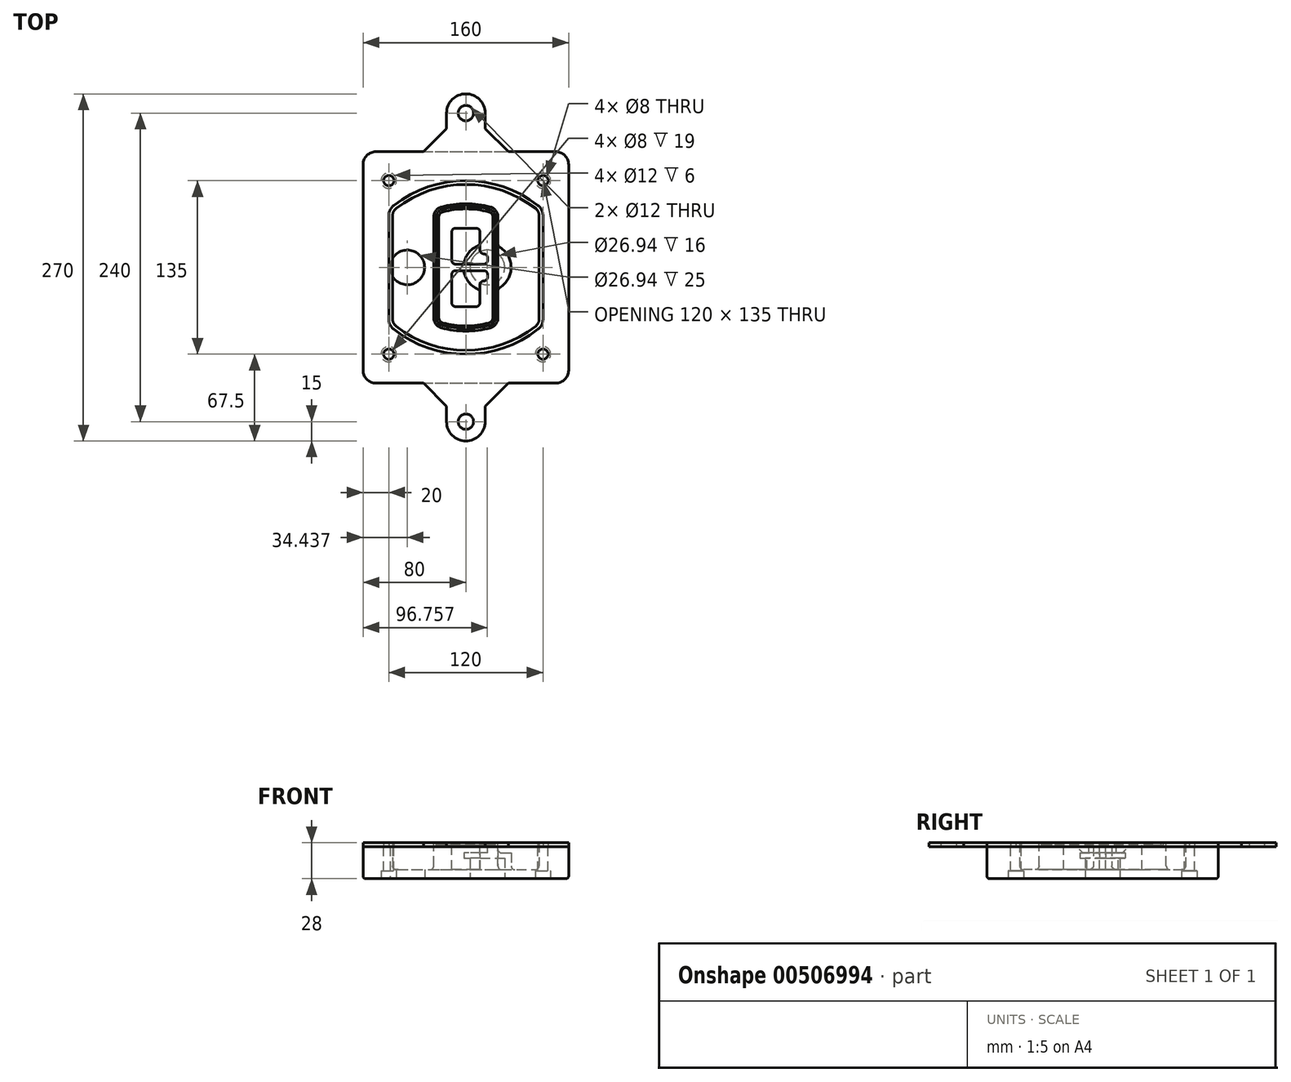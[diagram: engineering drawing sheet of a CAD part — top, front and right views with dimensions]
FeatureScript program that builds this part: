
annotation { "Feature Type Name" : "Feature", "Feature Type Description" : "" }
export const myFeature = defineFeature(function(context is Context, id is Id, definition is map)
    precondition{}
    {
        {
            var Q0;
            Q0=qCreatedBy(makeId("Top.planeOp"),FACE);
            var sketch = newSketch(context, id + "F0", { "sketchPlane" : qUnion([Q0])});
            skPoint(sketch, "E0.rect.middle", {"position": v(0, 0) * mm});
            skLineSegment(sketch, "E1.bottom", {"start": v(-70, -90) * mm, "end": v(70, -90) * mm});
            skLineSegment(sketch, "E1.top", {"start": v(-70, 90) * mm, "end": v(70, 90) * mm});
            skLineSegment(sketch, "E1.left", {"start": v(-80, -80) * mm, "end": v(-80, 80) * mm});
            skLineSegment(sketch, "E1.right", {"start": v(80, -80) * mm, "end": v(80, 80) * mm});
            skLineSegment(sketch, "E2", {"start": v(-80, 90) * mm, "end": v(80, -90) * mm, "construction": true});
            skLineSegment(sketch, "E3", {"start": v(80, 90) * mm, "end": v(-80, -90) * mm, "construction": true});
            skCircle(sketch, "E4", {"center": v(-60, 67.5) * mm, "radius": 4 * mm});
            skCircle(sketch, "E5", {"center": v(60, 67.5) * mm, "radius": 4 * mm});
            skCircle(sketch, "E6", {"center": v(60, -67.5) * mm, "radius": 4 * mm});
            skCircle(sketch, "E7", {"center": v(-60, -67.5) * mm, "radius": 4 * mm});
            skLineSegment(sketch, "E8", {"start": v(-60, 67.5) * mm, "end": v(60, 67.5) * mm, "construction": true});
            skLineSegment(sketch, "E9", {"start": v(60, 67.5) * mm, "end": v(60, -67.5) * mm, "construction": true});
            skLineSegment(sketch, "E10", {"start": v(60, -67.5) * mm, "end": v(-60, -67.5) * mm, "construction": true});
            skLineSegment(sketch, "E11", {"start": v(-60, -67.5) * mm, "end": v(-60, 67.5) * mm, "construction": true});
            skLineSegment(sketch, "E12", {"start": v(-60, 40.3) * mm, "end": v(-60, -40.3) * mm});
            skLineSegment(sketch, "E13", {"start": v(60, 40.3) * mm, "end": v(60, -40.3) * mm});
            skArc(sketch, "E14", {"start": v(56.15, 48.18) * mm, "mid": v(0, 67.5) * mm, "end": v(-56.15, 48.18) * mm});
            skArc(sketch, "E15", {"start": v(-56.15, -48.18) * mm, "mid": v(0, -67.5) * mm, "end": v(56.15, -48.18) * mm});
            skLineSegment(sketch, "E16", {"start": v(-60, 0) * mm, "end": v(60, 0) * mm, "construction": true});
            skPoint(sketch, "E17.visualSharp", {"position": v(-60, -45) * mm});
            skArc(sketch, "E17.filletArc", {"start": v(-60, -40.3) * mm, "mid": v(-58.99, -44.68) * mm, "end": v(-56.15, -48.18) * mm});
            skPoint(sketch, "E18.visualSharp", {"position": v(-60, 45) * mm});
            skArc(sketch, "E18.filletArc", {"start": v(-56.15, 48.18) * mm, "mid": v(-58.99, 44.68) * mm, "end": v(-60, 40.3) * mm});
            skPoint(sketch, "E19.visualSharp", {"position": v(60, 45) * mm});
            skArc(sketch, "E19.filletArc", {"start": v(60, 40.3) * mm, "mid": v(58.99, 44.68) * mm, "end": v(56.15, 48.18) * mm});
            skPoint(sketch, "E20.visualSharp", {"position": v(60, -45) * mm});
            skArc(sketch, "E20.filletArc", {"start": v(56.15, -48.18) * mm, "mid": v(58.99, -44.68) * mm, "end": v(60, -40.3) * mm});
            skPoint(sketch, "E21.visualSharp", {"position": v(-80, 90) * mm});
            skArc(sketch, "E21.filletArc", {"start": v(-70, 90) * mm, "mid": v(-77.07, 87.07) * mm, "end": v(-80, 80) * mm});
            skPoint(sketch, "E22.visualSharp", {"position": v(80, 90) * mm});
            skArc(sketch, "E22.filletArc", {"start": v(80, 80) * mm, "mid": v(77.07, 87.07) * mm, "end": v(70, 90) * mm});
            skPoint(sketch, "E23.visualSharp", {"position": v(80, -90) * mm});
            skArc(sketch, "E23.filletArc", {"start": v(70, -90) * mm, "mid": v(77.07, -87.07) * mm, "end": v(80, -80) * mm});
            skPoint(sketch, "E24.visualSharp", {"position": v(-80, -90) * mm});
            skArc(sketch, "E24.filletArc", {"start": v(-80, -80) * mm, "mid": v(-77.07, -87.07) * mm, "end": v(-70, -90) * mm});
            skArc(sketch, "E25.0", {"start": v(57, 40.3) * mm, "mid": v(56.3, 43.36) * mm, "end": v(54.3, 45.81) * mm});
            skLineSegment(sketch, "E25.1", {"start": v(57, 40.3) * mm, "end": v(57, -40.3) * mm});
            skArc(sketch, "E25.2", {"start": v(54.3, -45.81) * mm, "mid": v(56.3, -43.36) * mm, "end": v(57, -40.3) * mm});
            skArc(sketch, "E25.3", {"start": v(-54.3, -45.81) * mm, "mid": v(0, -64.5) * mm, "end": v(54.3, -45.81) * mm});
            skArc(sketch, "E25.4", {"start": v(-57, -40.3) * mm, "mid": v(-56.3, -43.36) * mm, "end": v(-54.3, -45.81) * mm});
            skArc(sketch, "E25.5", {"start": v(54.3, 45.81) * mm, "mid": v(0, 64.5) * mm, "end": v(-54.3, 45.81) * mm});
            skLineSegment(sketch, "E25.6", {"start": v(-57, 40.3) * mm, "end": v(-57, -40.3) * mm});
            skArc(sketch, "E25.7", {"start": v(-54.3, 45.81) * mm, "mid": v(-56.3, 43.36) * mm, "end": v(-57, 40.3) * mm});
            skArc(sketch, "E26.0", {"start": v(-58.62, 51.33) * mm, "mid": v(-62.58, 46.43) * mm, "end": v(-64, 40.3) * mm});
            skArc(sketch, "E26.1", {"start": v(58.62, 51.33) * mm, "mid": v(0, 71.5) * mm, "end": v(-58.62, 51.33) * mm});
            skArc(sketch, "E26.2", {"start": v(64, 40.3) * mm, "mid": v(62.58, 46.43) * mm, "end": v(58.62, 51.33) * mm});
            skLineSegment(sketch, "E26.3", {"start": v(64, 40.3) * mm, "end": v(64, -40.3) * mm});
            skArc(sketch, "E26.4", {"start": v(58.62, -51.33) * mm, "mid": v(62.58, -46.43) * mm, "end": v(64, -40.3) * mm});
            skLineSegment(sketch, "E26.5", {"start": v(-64, 40.3) * mm, "end": v(-64, -40.3) * mm});
            skArc(sketch, "E26.6", {"start": v(-58.62, -51.33) * mm, "mid": v(0, -71.5) * mm, "end": v(58.62, -51.33) * mm});
            skArc(sketch, "E26.7", {"start": v(-64, -40.3) * mm, "mid": v(-62.58, -46.43) * mm, "end": v(-58.62, -51.33) * mm});
            skSolve(sketch);
        }
        {
            var Q0;
            Q0=makeQuery(id+"F0.imprint","IMPRINT",FACE,{"disambiguationData":[TD([[makeQuery(id+"F0.imprint","IMPRINT",EDGE,{"derivedFrom":sQuery(id+"F0.wireOp",EDGE,"E1.bottom")}),1.0]])]});
            var Q1;
            Q1=makeQuery(id+"F0.imprint","IMPRINT",FACE,{"disambiguationData":[TD([[makeQuery(id+"F0.imprint","IMPRINT",EDGE,{"derivedFrom":sQuery(id+"F0.wireOp",EDGE,"E12")}),1.0]])]});
            var Q2;
            Q2=makeQuery(id+"F0.imprint","IMPRINT",FACE,{"disambiguationData":[TD([[makeQuery(id+"F0.imprint","IMPRINT",EDGE,{"derivedFrom":sQuery(id+"F0.wireOp",EDGE,"E25.0")}),1.0]])]});
            var Q3;
            Q3=makeQuery(id+"F0.imprint","IMPRINT",FACE,{"disambiguationData":[TD([[makeQuery(id+"F0.imprint","IMPRINT",EDGE,{"derivedFrom":sQuery(id+"F0.wireOp",EDGE,"E12")}),-1.0]])]});
            extrude(context, id + "F1", {"entities" : qUnion([Q0, Q1, Q2, Q3]), "oppositeDirection" : true, "depth" : 25 * mm});
        }
        {
            var Q0;
            Q0=makeQuery(id+"F0.imprint","IMPRINT",FACE,{"disambiguationData":[TD([[makeQuery(id+"F0.imprint","IMPRINT",EDGE,{"derivedFrom":sQuery(id+"F0.wireOp",EDGE,"E12")}),1.0]])]});
            extrude(context, id + "F2", {"entities" : qUnion([Q0]), "operationType" : NewBodyOperationType.ADD, "depth" : 3 * mm});
        }
        {
            var Q0;
            Q0=makeQuery(id+"F0.imprint","IMPRINT",FACE,{"disambiguationData":[TD([[makeQuery(id+"F0.imprint","IMPRINT",EDGE,{"derivedFrom":sQuery(id+"F0.wireOp",EDGE,"E25.0")}),1.0]])]});
            extrude(context, id + "F3", {"entities" : qUnion([Q0]), "operationType" : NewBodyOperationType.REMOVE, "oppositeDirection" : true, "depth" : 18 * mm});
        }
        {
            var Q0;
            Q0=makeQuery(id+"F2.opExtrude","CAP_FACE",FACE,{"disambiguationData":[OSD([sQuery(id+"F0.wireOp",EDGE,"E12"),sQuery(id+"F0.wireOp",EDGE,"E13"),sQuery(id+"F0.wireOp",EDGE,"E14"),sQuery(id+"F0.wireOp",EDGE,"E15"),sQuery(id+"F0.wireOp",EDGE,"E17.filletArc"),sQuery(id+"F0.wireOp",EDGE,"E18.filletArc"),sQuery(id+"F0.wireOp",EDGE,"E19.filletArc"),sQuery(id+"F0.wireOp",EDGE,"E20.filletArc"),sQuery(id+"F0.wireOp",EDGE,"E25.0"),sQuery(id+"F0.wireOp",EDGE,"E25.1"),sQuery(id+"F0.wireOp",EDGE,"E25.2"),sQuery(id+"F0.wireOp",EDGE,"E25.3"),sQuery(id+"F0.wireOp",EDGE,"E25.4"),sQuery(id+"F0.wireOp",EDGE,"E25.5"),sQuery(id+"F0.wireOp",EDGE,"E25.6"),sQuery(id+"F0.wireOp",EDGE,"E25.7")])],"isStart":false});
            var sketch = newSketch(context, id + "F4", { "sketchPlane" : qUnion([Q0])});
            skArc(sketch, "E27.0", {"start": v(-19.08, -46.97) * mm, "mid": v(0, -49.5) * mm, "end": v(19.08, -46.97) * mm});
            skArc(sketch, "E28.0", {"start": v(19.08, 46.97) * mm, "mid": v(0, 49.5) * mm, "end": v(-19.08, 46.97) * mm});
            skLineSegment(sketch, "E29", {"start": v(-25, 39.25) * mm, "end": v(-25, -39.25) * mm});
            skLineSegment(sketch, "E30", {"start": v(25, 39.25) * mm, "end": v(25, -39.25) * mm});
            skLineSegment(sketch, "E31", {"start": v(-25, 45.1) * mm, "end": v(25, 45.1) * mm, "construction": true});
            skLineSegment(sketch, "E32", {"start": v(-25, -45.1) * mm, "end": v(25, -45.1) * mm, "construction": true});
            skPoint(sketch, "E33.visualSharp", {"position": v(-25, 45.1) * mm});
            skArc(sketch, "E33.filletArc", {"start": v(-19.08, 46.97) * mm, "mid": v(-23.35, 44.11) * mm, "end": v(-25, 39.25) * mm});
            skPoint(sketch, "E34.visualSharp", {"position": v(25, 45.1) * mm});
            skArc(sketch, "E34.filletArc", {"start": v(25, 39.25) * mm, "mid": v(23.35, 44.11) * mm, "end": v(19.08, 46.97) * mm});
            skPoint(sketch, "E35.visualSharp", {"position": v(25, -45.1) * mm});
            skArc(sketch, "E35.filletArc", {"start": v(19.08, -46.97) * mm, "mid": v(23.35, -44.11) * mm, "end": v(25, -39.25) * mm});
            skPoint(sketch, "E36.visualSharp", {"position": v(-25, -45.1) * mm});
            skArc(sketch, "E36.filletArc", {"start": v(-25, -39.25) * mm, "mid": v(-23.35, -44.11) * mm, "end": v(-19.08, -46.97) * mm});
            skArc(sketch, "E37.0", {"start": v(54.3, 45.81) * mm, "mid": v(0, 64.5) * mm, "end": v(-54.3, 45.81) * mm});
            skArc(sketch, "E37.1", {"start": v(-54.3, 45.81) * mm, "mid": v(-56.3, 43.36) * mm, "end": v(-57, 40.3) * mm});
            skLineSegment(sketch, "E37.2", {"start": v(-57, 40.3) * mm, "end": v(-57, -40.3) * mm});
            skArc(sketch, "E37.3", {"start": v(-57, -40.3) * mm, "mid": v(-56.3, -43.36) * mm, "end": v(-54.3, -45.81) * mm});
            skArc(sketch, "E37.4", {"start": v(-54.3, -45.81) * mm, "mid": v(0, -64.5) * mm, "end": v(54.3, -45.81) * mm});
            skArc(sketch, "E37.5", {"start": v(54.3, -45.81) * mm, "mid": v(56.3, -43.36) * mm, "end": v(57, -40.3) * mm});
            skLineSegment(sketch, "E37.6", {"start": v(57, 40.3) * mm, "end": v(57, -40.3) * mm});
            skArc(sketch, "E37.7", {"start": v(57, 40.3) * mm, "mid": v(56.3, 43.36) * mm, "end": v(54.3, 45.81) * mm});
            skLineSegment(sketch, "E38.0", {"start": v(23, 39.25) * mm, "end": v(23, -39.25) * mm});
            skArc(sketch, "E38.1", {"start": v(18.56, -45.04) * mm, "mid": v(21.76, -42.9) * mm, "end": v(23, -39.25) * mm});
            skArc(sketch, "E38.2", {"start": v(-18.56, -45.04) * mm, "mid": v(0, -47.5) * mm, "end": v(18.56, -45.04) * mm});
            skArc(sketch, "E38.3", {"start": v(-23, -39.25) * mm, "mid": v(-21.76, -42.9) * mm, "end": v(-18.56, -45.04) * mm});
            skLineSegment(sketch, "E38.4", {"start": v(-23, 39.25) * mm, "end": v(-23, -39.25) * mm});
            skArc(sketch, "E38.5", {"start": v(23, 39.25) * mm, "mid": v(21.76, 42.9) * mm, "end": v(18.56, 45.04) * mm});
            skArc(sketch, "E38.6", {"start": v(-18.56, 45.04) * mm, "mid": v(-21.76, 42.9) * mm, "end": v(-23, 39.25) * mm});
            skArc(sketch, "E38.7", {"start": v(18.56, 45.04) * mm, "mid": v(0, 47.5) * mm, "end": v(-18.56, 45.04) * mm});
            skArc(sketch, "E39.0", {"start": v(21, 39.25) * mm, "mid": v(20.18, 41.68) * mm, "end": v(18.04, 43.1) * mm});
            skLineSegment(sketch, "E39.1", {"start": v(21, 39.25) * mm, "end": v(21, -39.25) * mm});
            skArc(sketch, "E39.2", {"start": v(18.04, -43.1) * mm, "mid": v(20.18, -41.68) * mm, "end": v(21, -39.25) * mm});
            skArc(sketch, "E39.3", {"start": v(-18.04, -43.1) * mm, "mid": v(0, -45.5) * mm, "end": v(18.04, -43.1) * mm});
            skArc(sketch, "E39.4", {"start": v(-21, -39.25) * mm, "mid": v(-20.18, -41.68) * mm, "end": v(-18.04, -43.1) * mm});
            skArc(sketch, "E39.5", {"start": v(18.04, 43.1) * mm, "mid": v(0, 45.5) * mm, "end": v(-18.04, 43.1) * mm});
            skLineSegment(sketch, "E39.6", {"start": v(-21, 39.25) * mm, "end": v(-21, -39.25) * mm});
            skArc(sketch, "E39.7", {"start": v(-18.04, 43.1) * mm, "mid": v(-20.18, 41.68) * mm, "end": v(-21, 39.25) * mm});
            skLineSegment(sketch, "E40", {"start": v(-25, 0) * mm, "end": v(25, 0) * mm, "construction": true});
            skLineSegment(sketch, "E41", {"start": v(-11, 5.5) * mm, "end": v(-11, 27.5) * mm});
            skLineSegment(sketch, "E42", {"start": v(-8, 30.5) * mm, "end": v(8, 30.5) * mm});
            skLineSegment(sketch, "E43", {"start": v(11, 27.5) * mm, "end": v(11, 13.5) * mm});
            skLineSegment(sketch, "E44", {"start": v(14, 10.5) * mm, "end": v(14, 10.5) * mm});
            skLineSegment(sketch, "E45", {"start": v(17, 7.5) * mm, "end": v(17, 5.5) * mm});
            skLineSegment(sketch, "E46", {"start": v(14, 2.5) * mm, "end": v(-8, 2.5) * mm});
            skPoint(sketch, "E47.visualSharp", {"position": v(-11, 30.5) * mm});
            skArc(sketch, "E47.filletArc", {"start": v(-8, 30.5) * mm, "mid": v(-10.12, 29.62) * mm, "end": v(-11, 27.5) * mm});
            skPoint(sketch, "E48.visualSharp", {"position": v(11, 30.5) * mm});
            skArc(sketch, "E48.filletArc", {"start": v(11, 27.5) * mm, "mid": v(10.12, 29.62) * mm, "end": v(8, 30.5) * mm});
            skPoint(sketch, "E49.visualSharp", {"position": v(11, 10.5) * mm});
            skArc(sketch, "E49.filletArc", {"start": v(11, 13.5) * mm, "mid": v(11.88, 11.38) * mm, "end": v(14, 10.5) * mm});
            skPoint(sketch, "E50.visualSharp", {"position": v(17, 10.5) * mm});
            skArc(sketch, "E50.filletArc", {"start": v(17, 7.5) * mm, "mid": v(16.12, 9.62) * mm, "end": v(14, 10.5) * mm});
            skPoint(sketch, "E51.visualSharp", {"position": v(17, 2.5) * mm});
            skArc(sketch, "E51.filletArc", {"start": v(14, 2.5) * mm, "mid": v(16.12, 3.38) * mm, "end": v(17, 5.5) * mm});
            skPoint(sketch, "E52.visualSharp", {"position": v(-11, 2.5) * mm});
            skArc(sketch, "E52.filletArc", {"start": v(-11, 5.5) * mm, "mid": v(-10.12, 3.38) * mm, "end": v(-8, 2.5) * mm});
            skLineSegment(sketch, "E53.0.MirrorCS", {"start": v(14, -2.5) * mm, "end": v(-8, -2.5) * mm});
            skArc(sketch, "E54.0.MirrorCS", {"start": v(-11, -5.5) * mm, "mid": v(-10.12, -3.38) * mm, "end": v(-8, -2.5) * mm});
            skLineSegment(sketch, "E55.0.MirrorCS", {"start": v(-11, -5.5) * mm, "end": v(-11, -27.5) * mm});
            skArc(sketch, "E56.0.MirrorCS", {"start": v(-8, -30.5) * mm, "mid": v(-10.12, -29.62) * mm, "end": v(-11, -27.5) * mm});
            skLineSegment(sketch, "E57.0.MirrorCS", {"start": v(-8, -30.5) * mm, "end": v(8, -30.5) * mm});
            skArc(sketch, "E58.0.MirrorCS", {"start": v(11, -27.5) * mm, "mid": v(10.12, -29.62) * mm, "end": v(8, -30.5) * mm});
            skLineSegment(sketch, "E59.0.MirrorCS", {"start": v(11, -27.5) * mm, "end": v(11, -13.5) * mm});
            skArc(sketch, "E60.0.MirrorCS", {"start": v(11, -13.5) * mm, "mid": v(11.88, -11.38) * mm, "end": v(14, -10.5) * mm});
            skArc(sketch, "E61.0.MirrorCS", {"start": v(17, -7.5) * mm, "mid": v(16.12, -9.62) * mm, "end": v(14, -10.5) * mm});
            skLineSegment(sketch, "E62.0.MirrorCS", {"start": v(17, -7.5) * mm, "end": v(17, -5.5) * mm});
            skArc(sketch, "E63.0.MirrorCS", {"start": v(14, -2.5) * mm, "mid": v(16.12, -3.38) * mm, "end": v(17, -5.5) * mm});
            skSolve(sketch);
        }
        {
            var Q0;
            Q0=makeQuery(id+"F4.imprint","IMPRINT",FACE,{"disambiguationData":[TD([[makeQuery(id+"F4.imprint","IMPRINT",EDGE,{"derivedFrom":sQuery(id+"F4.wireOp",EDGE,"E27.0")}),1.0]])]});
            var Q1;
            Q1=makeQuery(id+"F4.imprint","IMPRINT",FACE,{"disambiguationData":[TD([[makeQuery(id+"F4.imprint","IMPRINT",EDGE,{"derivedFrom":sQuery(id+"F4.wireOp",EDGE,"E38.0")}),-1.0]])]});
            var Q2;
            Q2=makeQuery(id+"F4.imprint","IMPRINT",FACE,{"disambiguationData":[TD([[makeQuery(id+"F4.imprint","IMPRINT",EDGE,{"derivedFrom":sQuery(id+"F4.wireOp",EDGE,"E39.0")}),1.0]])]});
            extrude(context, id + "F5", {"entities" : qUnion([Q0, Q1, Q2]), "operationType" : NewBodyOperationType.ADD, "endBound" : BoundingType.UP_TO_NEXT, "oppositeDirection" : true, "depth" : 25 * mm});
        }
        {
            var Q0;
            Q0=makeQuery(id+"F4.imprint","IMPRINT",FACE,{"disambiguationData":[TD([[makeQuery(id+"F4.imprint","IMPRINT",EDGE,{"derivedFrom":sQuery(id+"F4.wireOp",EDGE,"E38.0")}),-1.0]])]});
            extrude(context, id + "F6", {"entities" : qUnion([Q0]), "operationType" : NewBodyOperationType.REMOVE, "oppositeDirection" : true, "depth" : 2 * mm});
        }
        {
            var Q0;
            Q0=makeQuery(id+"F1.opExtrude","CAP_FACE",FACE,{"disambiguationData":[OSD([sQuery(id+"F0.wireOp",EDGE,"E1.bottom"),sQuery(id+"F0.wireOp",EDGE,"E1.top"),sQuery(id+"F0.wireOp",EDGE,"E1.left"),sQuery(id+"F0.wireOp",EDGE,"E1.right"),sQuery(id+"F0.wireOp",EDGE,"E4"),sQuery(id+"F0.wireOp",EDGE,"E5"),sQuery(id+"F0.wireOp",EDGE,"E6"),sQuery(id+"F0.wireOp",EDGE,"E7"),sQuery(id+"F0.wireOp",EDGE,"E21.filletArc"),sQuery(id+"F0.wireOp",EDGE,"E22.filletArc"),sQuery(id+"F0.wireOp",EDGE,"E23.filletArc"),sQuery(id+"F0.wireOp",EDGE,"E24.filletArc")])],"isStart":false});
            var sketch = newSketch(context, id + "F7", { "sketchPlane" : qUnion([Q0])});
            skCircle(sketch, "E64", {"center": v(16.76, 0) * mm, "radius": 13.47 * mm});
            skCircle(sketch, "E65", {"center": v(-45.56, 0) * mm, "radius": 13.47 * mm});
            skLineSegment(sketch, "E66", {"start": v(80, 0) * mm, "end": v(-80, 0) * mm});
            skCircle(sketch, "E67", {"center": v(16.76, 0) * mm, "radius": 18.47 * mm});
            skCircle(sketch, "E68", {"center": v(60, -67.5) * mm, "radius": 6 * mm});
            skCircle(sketch, "E69", {"center": v(-60, -67.5) * mm, "radius": 6 * mm});
            skCircle(sketch, "E70", {"center": v(-60, 67.5) * mm, "radius": 6 * mm});
            skCircle(sketch, "E71", {"center": v(60, 67.5) * mm, "radius": 6 * mm});
            skSolve(sketch);
        }
        {
            var Q0;
            {var subQ1=sQuery(id+"F7.wireOp",EDGE,"E66");var subQ4=sQuery(id+"F7.wireOp",EDGE,"E64");var subQ6=makeQuery(id+"F7.imprint","INTERSECT",VERTEX,{"disambiguationData":[OD(0.0)],"derivedFrom":[subQ4,subQ1]});Q0=makeQuery(id+"F7.imprint","IMPRINT",FACE,{"disambiguationData":[TD([[makeQuery(id+"F7.imprint","IMPRINT",EDGE,{"disambiguationData":[TD([[subQ6,-1.0]])],"derivedFrom":subQ4}),-1.0]])]});}
            var Q1;
            {var subQ0=sQuery(id+"F7.wireOp",EDGE,"E66");var subQ1=sQuery(id+"F7.wireOp",EDGE,"E64");var subQ3=makeQuery(id+"F7.imprint","INTERSECT",VERTEX,{"disambiguationData":[OD(0.0)],"derivedFrom":[subQ1,subQ0]});Q1=makeQuery(id+"F7.imprint","IMPRINT",FACE,{"disambiguationData":[TD([[makeQuery(id+"F7.imprint","IMPRINT",EDGE,{"disambiguationData":[TD([[subQ3,-1.0]])],"derivedFrom":subQ1}),1.0]])]});}
            var Q2;
            {var subQ0=sQuery(id+"F7.wireOp",EDGE,"E66");var subQ1=sQuery(id+"F7.wireOp",EDGE,"E64");var subQ3=makeQuery(id+"F7.imprint","INTERSECT",VERTEX,{"disambiguationData":[OD(0.0)],"derivedFrom":[subQ1,subQ0]});Q2=makeQuery(id+"F7.imprint","IMPRINT",FACE,{"disambiguationData":[TD([[makeQuery(id+"F7.imprint","IMPRINT",EDGE,{"disambiguationData":[TD([[subQ3,1.0]])],"derivedFrom":subQ1}),1.0]])]});}
            var Q3;
            {var subQ1=sQuery(id+"F7.wireOp",EDGE,"E66");var subQ4=sQuery(id+"F7.wireOp",EDGE,"E64");var subQ6=makeQuery(id+"F7.imprint","INTERSECT",VERTEX,{"disambiguationData":[OD(0.0)],"derivedFrom":[subQ4,subQ1]});Q3=makeQuery(id+"F7.imprint","IMPRINT",FACE,{"disambiguationData":[TD([[makeQuery(id+"F7.imprint","IMPRINT",EDGE,{"disambiguationData":[TD([[subQ6,1.0]])],"derivedFrom":subQ4}),-1.0]])]});}
            extrude(context, id + "F8", {"entities" : qUnion([Q0, Q1, Q2, Q3]), "operationType" : NewBodyOperationType.ADD, "oppositeDirection" : true, "depth" : 20 * mm});
        }
        {
            var Q0;
            {var subQ0=sQuery(id+"F7.wireOp",EDGE,"E66");var subQ1=sQuery(id+"F7.wireOp",EDGE,"E64");var subQ3=makeQuery(id+"F7.imprint","INTERSECT",VERTEX,{"disambiguationData":[OD(0.0)],"derivedFrom":[subQ1,subQ0]});Q0=makeQuery(id+"F7.imprint","IMPRINT",FACE,{"disambiguationData":[TD([[makeQuery(id+"F7.imprint","IMPRINT",EDGE,{"disambiguationData":[TD([[subQ3,-1.0]])],"derivedFrom":subQ1}),1.0]])]});}
            var Q1;
            {var subQ0=sQuery(id+"F7.wireOp",EDGE,"E66");var subQ1=sQuery(id+"F7.wireOp",EDGE,"E64");var subQ3=makeQuery(id+"F7.imprint","INTERSECT",VERTEX,{"disambiguationData":[OD(0.0)],"derivedFrom":[subQ1,subQ0]});Q1=makeQuery(id+"F7.imprint","IMPRINT",FACE,{"disambiguationData":[TD([[makeQuery(id+"F7.imprint","IMPRINT",EDGE,{"disambiguationData":[TD([[subQ3,1.0]])],"derivedFrom":subQ1}),1.0]])]});}
            extrude(context, id + "F9", {"entities" : qUnion([Q0, Q1]), "operationType" : NewBodyOperationType.REMOVE, "oppositeDirection" : true, "depth" : 16 * mm});
        }
        {
            var Q0;
            {var subQ0=sQuery(id+"F7.wireOp",EDGE,"E66");var subQ1=sQuery(id+"F7.wireOp",EDGE,"E65");var subQ3=makeQuery(id+"F7.imprint","INTERSECT",VERTEX,{"disambiguationData":[OD(0.0)],"derivedFrom":[subQ1,subQ0]});Q0=makeQuery(id+"F7.imprint","IMPRINT",FACE,{"disambiguationData":[TD([[makeQuery(id+"F7.imprint","IMPRINT",EDGE,{"disambiguationData":[TD([[subQ3,-1.0]])],"derivedFrom":subQ1}),1.0]])]});}
            var Q1;
            {var subQ0=sQuery(id+"F7.wireOp",EDGE,"E66");var subQ1=sQuery(id+"F7.wireOp",EDGE,"E65");var subQ3=makeQuery(id+"F7.imprint","INTERSECT",VERTEX,{"disambiguationData":[OD(0.0)],"derivedFrom":[subQ1,subQ0]});Q1=makeQuery(id+"F7.imprint","IMPRINT",FACE,{"disambiguationData":[TD([[makeQuery(id+"F7.imprint","IMPRINT",EDGE,{"disambiguationData":[TD([[subQ3,1.0]])],"derivedFrom":subQ1}),1.0]])]});}
            extrude(context, id + "F10", {"entities" : qUnion([Q0, Q1]), "operationType" : NewBodyOperationType.REMOVE, "oppositeDirection" : true, "depth" : 25 * mm});
        }
        {
            var Q0;
            Q0=makeQuery(id+"F7.imprint","IMPRINT",FACE,{"disambiguationData":[TD([[makeQuery(id+"F7.imprint","IMPRINT",EDGE,{"derivedFrom":sQuery(id+"F7.wireOp",EDGE,"E68")}),1.0]])]});
            var Q1;
            Q1=makeQuery(id+"F7.imprint","IMPRINT",FACE,{"disambiguationData":[TD([[makeQuery(id+"F7.imprint","IMPRINT",EDGE,{"derivedFrom":makeQuery(id+"F1.opExtrude","CAP_EDGE",EDGE,{"disambiguationData":[OSD([sQuery(id+"F0.wireOp",EDGE,"E5")])],"isStart":false})}),-1.0]])]});
            var Q2;
            Q2=makeQuery(id+"F7.imprint","IMPRINT",FACE,{"disambiguationData":[TD([[makeQuery(id+"F7.imprint","IMPRINT",EDGE,{"derivedFrom":sQuery(id+"F7.wireOp",EDGE,"E69")}),1.0]])]});
            var Q3;
            Q3=makeQuery(id+"F7.imprint","IMPRINT",FACE,{"disambiguationData":[TD([[makeQuery(id+"F7.imprint","IMPRINT",EDGE,{"derivedFrom":makeQuery(id+"F1.opExtrude","CAP_EDGE",EDGE,{"disambiguationData":[OSD([sQuery(id+"F0.wireOp",EDGE,"E4")])],"isStart":false})}),-1.0]])]});
            var Q4;
            Q4=makeQuery(id+"F7.imprint","IMPRINT",FACE,{"disambiguationData":[TD([[makeQuery(id+"F7.imprint","IMPRINT",EDGE,{"derivedFrom":sQuery(id+"F7.wireOp",EDGE,"E70")}),1.0]])]});
            var Q5;
            Q5=makeQuery(id+"F7.imprint","IMPRINT",FACE,{"disambiguationData":[TD([[makeQuery(id+"F7.imprint","IMPRINT",EDGE,{"derivedFrom":makeQuery(id+"F1.opExtrude","CAP_EDGE",EDGE,{"disambiguationData":[OSD([sQuery(id+"F0.wireOp",EDGE,"E7")])],"isStart":false})}),-1.0]])]});
            var Q6;
            Q6=makeQuery(id+"F7.imprint","IMPRINT",FACE,{"disambiguationData":[TD([[makeQuery(id+"F7.imprint","IMPRINT",EDGE,{"derivedFrom":sQuery(id+"F7.wireOp",EDGE,"E71")}),1.0]])]});
            var Q7;
            Q7=makeQuery(id+"F7.imprint","IMPRINT",FACE,{"disambiguationData":[TD([[makeQuery(id+"F7.imprint","IMPRINT",EDGE,{"derivedFrom":makeQuery(id+"F1.opExtrude","CAP_EDGE",EDGE,{"disambiguationData":[OSD([sQuery(id+"F0.wireOp",EDGE,"E6")])],"isStart":false})}),-1.0]])]});
            extrude(context, id + "F11", {"entities" : qUnion([Q0, Q1, Q2, Q3, Q4, Q5, Q6, Q7]), "operationType" : NewBodyOperationType.REMOVE, "oppositeDirection" : true, "depth" : 6 * mm});
        }
        {
            var Q0;
            Q0=makeQuery(id+"F9.boolean.opBoolean","COPY",FACE,{"derivedFrom":makeQuery(id+"F9.opExtrude","CAP_FACE",FACE,{"disambiguationData":[OSD([sQuery(id+"F7.wireOp",EDGE,"E64")])],"isStart":false})});
            var sketch = newSketch(context, id + "F12", { "sketchPlane" : qUnion([Q0])});
            skArc(sketch, "E72.0", {"start": v(11, 17.55) * mm, "mid": v(2.57, 11.82) * mm, "end": v(-1.54, 2.5) * mm});
            skArc(sketch, "E72.1", {"start": v(-1.54, -2.5) * mm, "mid": v(2.57, -11.82) * mm, "end": v(11, -17.55) * mm});
            skLineSegment(sketch, "E73", {"start": v(-1.54, -2.5) * mm, "end": v(14, -2.5) * mm});
            skLineSegment(sketch, "E74.0", {"start": v(14, 2.5) * mm, "end": v(-1.54, 2.5) * mm});
            skArc(sketch, "E74.1", {"start": v(14, 2.5) * mm, "mid": v(16.12, 3.38) * mm, "end": v(17, 5.5) * mm});
            skLineSegment(sketch, "E74.2", {"start": v(17, 7.5) * mm, "end": v(17, 5.5) * mm});
            skArc(sketch, "E74.3", {"start": v(17, 7.5) * mm, "mid": v(16.12, 9.62) * mm, "end": v(14, 10.5) * mm});
            skArc(sketch, "E74.4", {"start": v(11, 13.5) * mm, "mid": v(11.88, 11.38) * mm, "end": v(14, 10.5) * mm});
            skLineSegment(sketch, "E74.5", {"start": v(11, 17.55) * mm, "end": v(11, 13.5) * mm});
            skLineSegment(sketch, "E74.7", {"start": v(14, -2.5) * mm, "end": v(-1.54, -2.5) * mm});
            skArc(sketch, "E74.8", {"start": v(14, -2.5) * mm, "mid": v(16.12, -3.38) * mm, "end": v(17, -5.5) * mm});
            skLineSegment(sketch, "E74.9", {"start": v(17, -7.5) * mm, "end": v(17, -5.5) * mm});
            skArc(sketch, "E74.10", {"start": v(17, -7.5) * mm, "mid": v(16.12, -9.62) * mm, "end": v(14, -10.5) * mm});
            skArc(sketch, "E74.11", {"start": v(11, -13.5) * mm, "mid": v(11.88, -11.38) * mm, "end": v(14, -10.5) * mm});
            skLineSegment(sketch, "E74.12", {"start": v(11, -17.55) * mm, "end": v(11, -13.5) * mm});
            skPoint(sketch, "E75.orphan", {"position": v(11, -27.5) * mm});
            skPoint(sketch, "E76.orphan", {"position": v(-8, -2.5) * mm});
            skPoint(sketch, "E77.orphan", {"position": v(-8, 2.5) * mm});
            skPoint(sketch, "E78.orphan", {"position": v(11, 27.5) * mm});
            skSolve(sketch);
        }
        {
            var Q0;
            {var subQ7=sQuery(id+"F12.wireOp",EDGE,"E72.0");var subQ14=sQuery(id+"F12.wireOp",EDGE,"E72.1");var subQ16=sQuery(id+"F12.wireOp",EDGE,"E74.1");var subQ18=sQuery(id+"F12.wireOp",EDGE,"E74.8");Q0=qUnion([makeQuery(id+"F12.imprint","IMPRINT",FACE,{"disambiguationData":[TD([[makeQuery(id+"F12.imprint","IMPRINT",EDGE,{"derivedFrom":subQ7}),1.0]])]}),makeQuery(id+"F12.imprint","IMPRINT",FACE,{"disambiguationData":[TD([[makeQuery(id+"F12.imprint","IMPRINT",EDGE,{"derivedFrom":subQ14}),1.0]])]}),makeQuery(id+"F12.imprint","IMPRINT",FACE,{"disambiguationData":[TD([[makeQuery(id+"F12.imprint","IMPRINT",EDGE,{"derivedFrom":subQ16}),1.0]])]}),makeQuery(id+"F12.imprint","IMPRINT",FACE,{"disambiguationData":[TD([[makeQuery(id+"F12.imprint","IMPRINT",EDGE,{"derivedFrom":subQ18}),-1.0]])]})]);}
            var Q1;
            Q1=makeQuery(id+"F5.boolean.opBoolean","SPLIT",FACE,{"disambiguationData":[TD([makeQuery(id+"F5.opExtrude","SWEPT_FACE",FACE,{"disambiguationData":[OSD([sQuery(id+"F4.wireOp",EDGE,"E41")])]})])],"derivedFrom":makeQuery(id+"F3.boolean.opBoolean","COPY",FACE,{"derivedFrom":makeQuery(id+"F3.opExtrude","CAP_FACE",FACE,{"disambiguationData":[OSD([sQuery(id+"F0.wireOp",EDGE,"E25.0"),sQuery(id+"F0.wireOp",EDGE,"E25.1"),sQuery(id+"F0.wireOp",EDGE,"E25.2"),sQuery(id+"F0.wireOp",EDGE,"E25.3"),sQuery(id+"F0.wireOp",EDGE,"E25.4"),sQuery(id+"F0.wireOp",EDGE,"E25.5"),sQuery(id+"F0.wireOp",EDGE,"E25.6"),sQuery(id+"F0.wireOp",EDGE,"E25.7")])],"isStart":false})})});
            extrude(context, id + "F13", {"entities" : qUnion([Q0]), "operationType" : NewBodyOperationType.REMOVE, "endBound" : BoundingType.UP_TO_SURFACE, "endBoundEntityFace" : qUnion([Q1]), "depth" : 25 * mm});
        }
        {
            var Q0;
            Q0=makeQuery(id+"F3.boolean.opBoolean","COPY",EDGE,{"derivedFrom":makeQuery(id+"F3.opExtrude","CAP_EDGE",EDGE,{"disambiguationData":[OSD([sQuery(id+"F0.wireOp",EDGE,"E25.6")])],"isStart":false})});
            var Q1;
            Q1=makeQuery(id+"F8.boolean.opBoolean","INTERSECT",EDGE,{"derivedFrom":[makeQuery(id+"F5.opExtrude","SWEPT_FACE",FACE,{"disambiguationData":[OSD([sQuery(id+"F4.wireOp",EDGE,"E30")])]}),makeQuery(id+"F8.opExtrude","CAP_FACE",FACE,{"disambiguationData":[OSD([sQuery(id+"F7.wireOp",EDGE,"E67")])],"isStart":false})]});
            var Q2;
            Q2=makeQuery(id+"F8.boolean.opBoolean","INTERSECT",EDGE,{"disambiguationData":[OD(1.0)],"derivedFrom":[makeQuery(id+"F5.opExtrude","SWEPT_FACE",FACE,{"disambiguationData":[OSD([sQuery(id+"F4.wireOp",EDGE,"E30")])]}),makeQuery(id+"F8.opExtrude","SWEPT_FACE",FACE,{"disambiguationData":[OSD([sQuery(id+"F7.wireOp",EDGE,"E67")])]})]});
            var Q3;
            {var subQ0=sQuery(id+"F4.wireOp",EDGE,"E30");Q3=makeQuery(id+"F8.boolean.opBoolean","SPLIT",EDGE,{"disambiguationData":[TD([makeQuery(id+"F5.opExtrude","SWEPT_FACE",FACE,{"disambiguationData":[OSD([sQuery(id+"F4.wireOp",EDGE,"E35.filletArc")])]})])],"derivedFrom":makeQuery(id+"F5.opExtrude","CAP_EDGE",EDGE,{"disambiguationData":[OSD([subQ0])],"isStart":false})});}
            var Q4;
            {var subQ0=sQuery(id+"F0.wireOp",EDGE,"E25.7");var subQ1=sQuery(id+"F0.wireOp",EDGE,"E25.1");var subQ2=sQuery(id+"F0.wireOp",EDGE,"E25.6");var subQ3=sQuery(id+"F0.wireOp",EDGE,"E25.5");var subQ4=sQuery(id+"F0.wireOp",EDGE,"E25.4");var subQ5=sQuery(id+"F0.wireOp",EDGE,"E25.0");var subQ6=sQuery(id+"F0.wireOp",EDGE,"E25.2");var subQ7=sQuery(id+"F0.wireOp",EDGE,"E25.3");Q4=makeQuery(id+"F8.boolean.opBoolean","INTERSECT",EDGE,{"derivedFrom":[makeQuery(id+"F5.boolean.opBoolean","SPLIT",FACE,{"disambiguationData":[TD([makeQuery(id+"F2.opExtrude","SWEPT_FACE",FACE,{"disambiguationData":[OSD([subQ5])]})])],"derivedFrom":makeQuery(id+"F3.boolean.opBoolean","COPY",FACE,{"derivedFrom":makeQuery(id+"F3.opExtrude","CAP_FACE",FACE,{"disambiguationData":[OSD([subQ5,subQ1,subQ6,subQ7,subQ4,subQ3,subQ2,subQ0])],"isStart":false})})}),makeQuery(id+"F8.opExtrude","SWEPT_FACE",FACE,{"disambiguationData":[OSD([sQuery(id+"F7.wireOp",EDGE,"E67")])]})]});}
            var Q5;
            Q5=makeQuery(id+"F8.boolean.opBoolean","INTERSECT",EDGE,{"disambiguationData":[OD(0.0)],"derivedFrom":[makeQuery(id+"F5.opExtrude","SWEPT_FACE",FACE,{"disambiguationData":[OSD([sQuery(id+"F4.wireOp",EDGE,"E30")])]}),makeQuery(id+"F8.opExtrude","SWEPT_FACE",FACE,{"disambiguationData":[OSD([sQuery(id+"F7.wireOp",EDGE,"E67")])]})]});
            fillet(context, id + "F14", {"entities" : qUnion([Q0, Q1, Q2, Q3, Q4, Q5]), "radius" : 3 * mm, "tangentPropagation" : true, "allowEdgeOverflow" : false});
        }
        {
            var Q0;
            Q0=makeQuery(id+"F1.opExtrude","CAP_EDGE",EDGE,{"disambiguationData":[OSD([sQuery(id+"F0.wireOp",EDGE,"E1.bottom")])],"isStart":false});
            fillet(context, id + "F15", {"entities" : qUnion([Q0]), "radius" : 2 * mm, "tangentPropagation" : true, "allowEdgeOverflow" : false});
        }
        {
            var Q0;
            {var subQ0=sQuery(id+"F0.wireOp",EDGE,"E21.filletArc");var subQ1=sQuery(id+"F0.wireOp",EDGE,"E7");var subQ2=sQuery(id+"F0.wireOp",EDGE,"E6");var subQ3=sQuery(id+"F0.wireOp",EDGE,"E5");var subQ4=sQuery(id+"F0.wireOp",EDGE,"E4");var subQ5=sQuery(id+"F0.wireOp",EDGE,"E22.filletArc");var subQ6=sQuery(id+"F0.wireOp",EDGE,"E1.bottom");var subQ7=sQuery(id+"F0.wireOp",EDGE,"E1.right");var subQ8=sQuery(id+"F0.wireOp",EDGE,"E1.top");var subQ9=sQuery(id+"F0.wireOp",EDGE,"E1.left");var subQ10=sQuery(id+"F0.wireOp",EDGE,"E23.filletArc");var subQ11=sQuery(id+"F0.wireOp",EDGE,"E24.filletArc");Q0=makeQuery(id+"F2.boolean.opBoolean","SPLIT",FACE,{"disambiguationData":[TD([makeQuery(id+"F1.opExtrude","SWEPT_FACE",FACE,{"disambiguationData":[OSD([subQ6])]})])],"derivedFrom":makeQuery(id+"F1.opExtrude","CAP_FACE",FACE,{"disambiguationData":[OSD([subQ6,subQ8,subQ9,subQ7,subQ4,subQ3,subQ2,subQ1,subQ0,subQ5,subQ10,subQ11])],"isStart":true})});}
            var sketch = newSketch(context, id + "F16", { "sketchPlane" : qUnion([Q0])});
            skCircle(sketch, "E79", {"center": v(0, 120) * mm, "radius": 6 * mm});
            skLineSegment(sketch, "E80", {"start": v(-33, 90) * mm, "end": v(-15, 108) * mm});
            skLineSegment(sketch, "E81", {"start": v(-15, 108) * mm, "end": v(-15, 120) * mm});
            skLineSegment(sketch, "E82", {"start": v(15, 108) * mm, "end": v(33, 90) * mm});
            skArc(sketch, "E83", {"start": v(-15, 120) * mm, "mid": v(0, 135) * mm, "end": v(15, 120) * mm});
            skLineSegment(sketch, "E84", {"start": v(15, 120) * mm, "end": v(15, 108) * mm});
            skLineSegment(sketch, "E85", {"start": v(-80, 0) * mm, "end": v(80, 0) * mm, "construction": true});
            skLineSegment(sketch, "E86", {"start": v(0, 120) * mm, "end": v(0, 90) * mm, "construction": true});
            skLineSegment(sketch, "E87.MirrorCS", {"start": v(0, -120) * mm, "end": v(0, -90) * mm, "construction": true});
            skLineSegment(sketch, "E88.MirrorCS", {"start": v(-33, -90) * mm, "end": v(-15, -108) * mm});
            skLineSegment(sketch, "E89.MirrorCS", {"start": v(-15, -108) * mm, "end": v(-15, -120) * mm});
            skArc(sketch, "E90.MirrorCS", {"start": v(-15, -120) * mm, "mid": v(0, -135) * mm, "end": v(15, -120) * mm});
            skCircle(sketch, "E91.MirrorC", {"center": v(0, -120) * mm, "radius": 6 * mm});
            skLineSegment(sketch, "E92.MirrorCS", {"start": v(15, -120) * mm, "end": v(15, -108) * mm});
            skLineSegment(sketch, "E93.MirrorCS", {"start": v(15, -108) * mm, "end": v(33, -90) * mm});
            skSolve(sketch);
        }
        {
            var Q0;
            Q0=makeQuery(id+"F16.imprint","IMPRINT",FACE,{"disambiguationData":[TD([[makeQuery(id+"F16.imprint","IMPRINT",EDGE,{"derivedFrom":sQuery(id+"F16.wireOp",EDGE,"E79")}),-1.0]])]});
            var Q1;
            {var subQ0=sQuery(id+"F16.wireOp",EDGE,"E88.MirrorCS");Q1=makeQuery(id+"F16.imprint","IMPRINT",FACE,{"disambiguationData":[TD([[makeQuery(id+"F16.imprint","IMPRINT",EDGE,{"derivedFrom":subQ0}),1.0]])]});}
            var Q2;
            Q2=makeQuery(id+"F16.imprint","IMPRINT",FACE,{"disambiguationData":[TD([[makeQuery(id+"F16.imprint","IMPRINT",EDGE,{"derivedFrom":makeQuery(id+"F1.opExtrude","CAP_EDGE",EDGE,{"disambiguationData":[OSD([sQuery(id+"F0.wireOp",EDGE,"E1.left")])],"isStart":true})}),-1.0]])]});
            var Q3;
            Q3=makeQuery(id+"F2.opExtrude","CAP_FACE",FACE,{"disambiguationData":[OSD([sQuery(id+"F0.wireOp",EDGE,"E12"),sQuery(id+"F0.wireOp",EDGE,"E13"),sQuery(id+"F0.wireOp",EDGE,"E14"),sQuery(id+"F0.wireOp",EDGE,"E15"),sQuery(id+"F0.wireOp",EDGE,"E17.filletArc"),sQuery(id+"F0.wireOp",EDGE,"E18.filletArc"),sQuery(id+"F0.wireOp",EDGE,"E19.filletArc"),sQuery(id+"F0.wireOp",EDGE,"E20.filletArc"),sQuery(id+"F0.wireOp",EDGE,"E25.0"),sQuery(id+"F0.wireOp",EDGE,"E25.1"),sQuery(id+"F0.wireOp",EDGE,"E25.2"),sQuery(id+"F0.wireOp",EDGE,"E25.3"),sQuery(id+"F0.wireOp",EDGE,"E25.4"),sQuery(id+"F0.wireOp",EDGE,"E25.5"),sQuery(id+"F0.wireOp",EDGE,"E25.6"),sQuery(id+"F0.wireOp",EDGE,"E25.7")])],"isStart":false});
            extrude(context, id + "F17", {"entities" : qUnion([Q0, Q1, Q2]), "endBound" : BoundingType.UP_TO_SURFACE, "endBoundEntityFace" : qUnion([Q3]), "depth" : 25 * mm, "offsetDistance" : 25 * mm});
        }
    });
